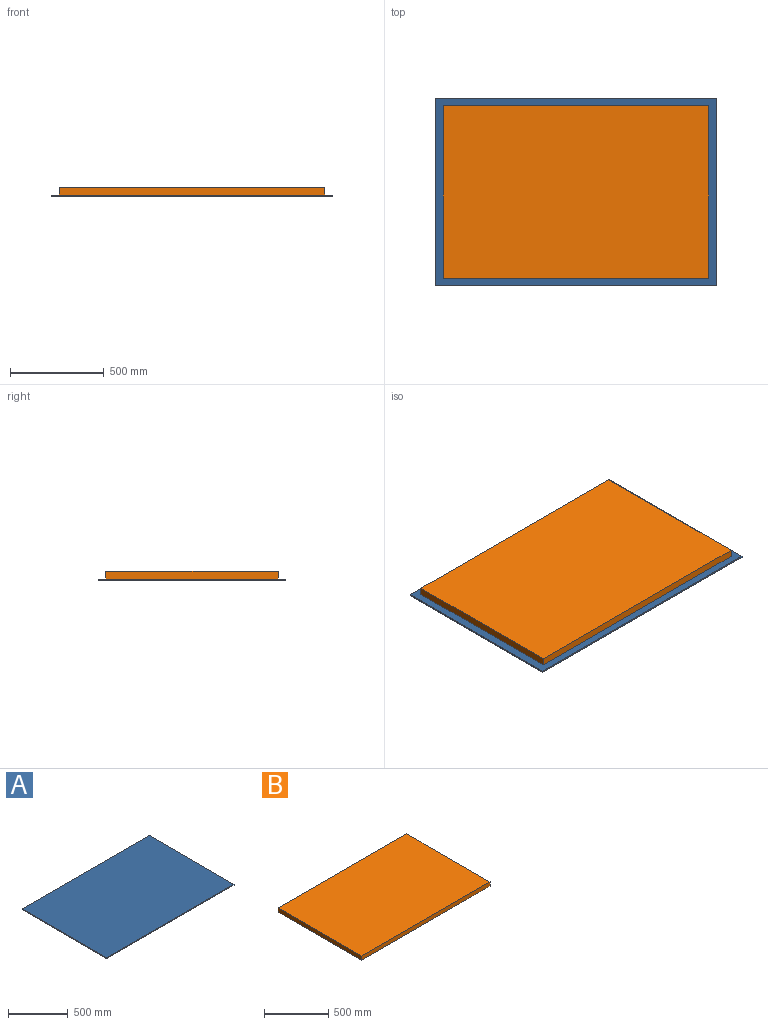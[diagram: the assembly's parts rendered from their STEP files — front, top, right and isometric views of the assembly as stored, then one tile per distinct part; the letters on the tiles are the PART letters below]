
ASSEMBLY  parts=2 mates=1
PART A: 6 faces, bbox 1500x1000x8 mm
  f0: plane 1500x8mm, normal (0,1,0), area 12000mm2, adj f1,f3,f4,f5
  f1: plane 1000x8mm, normal (-1,0,0), area 8000mm2, adj f0,f2,f4,f5
  f2: plane 1500x8mm, normal (0,-1,0), area 12000mm2, adj f1,f3,f4,f5
  f3: plane 1000x8mm, normal (1,0,0), area 8000mm2, adj f0,f2,f4,f5
  f4: plane 1500x1000mm, normal (0,0,1), area 1500000mm2, adj f0,f1,f2,f3
  f5: plane 1500x1000mm, normal (0,0,-1), area 1500000mm2, adj f0,f1,f2,f3
PART B: 6 faces, bbox 1415x920x40 mm
  f0: plane 1415x40mm, normal (0,1,0), area 56600mm2, adj f1,f3,f4,f5
  f1: plane 920x40mm, normal (-1,0,0), area 36800mm2, adj f0,f2,f4,f5
  f2: plane 1415x40mm, normal (0,-1,0), area 56600mm2, adj f1,f3,f4,f5
  f3: plane 920x40mm, normal (1,0,0), area 36800mm2, adj f0,f2,f4,f5
  f4: plane 1415x920mm, normal (0,0,1), area 1301800mm2, adj f0,f1,f2,f3
  f5: plane 1415x920mm, normal (0,0,-1), area 1301800mm2, adj f0,f1,f2,f3
PLACE A t=(178.09,-289.04,571.44)mm
PLACE B t=(186.14,-268.44,579.44)mm
MATE fastened A.f4 <-> B.f5  axis (0,0,1) through (-460.06,134.01,579.44)mm
